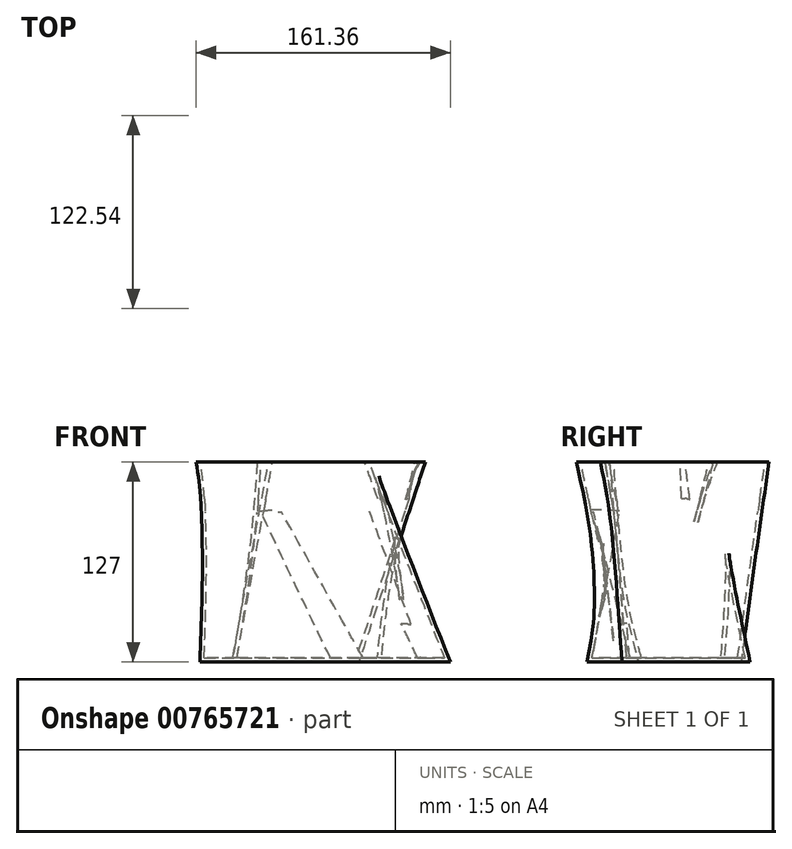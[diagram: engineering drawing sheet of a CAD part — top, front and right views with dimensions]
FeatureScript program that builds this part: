
annotation { "Feature Type Name" : "Feature", "Feature Type Description" : "" }
export const myFeature = defineFeature(function(context is Context, id is Id, definition is map)
    precondition{}
    {
        {
            var Q0;
            Q0=qCreatedBy(makeId("Top.planeOp"),FACE);
            var sketch = newSketch(context, id + "F0", { "sketchPlane" : qUnion([Q0])});
            skFitSpline(sketch, "E0", {"points": [v(0, 44.55) * mm, v(-25.5, 44.55) * mm, v(-44.65, 21.69) * mm, v(-46.6, 0) * mm, v(-53.63, -5.08) * mm, v(-65.55, -33.41) * mm, v(-34.3, -44.16) * mm, v(0, -50.02) * mm, v(31.36, -48.26) * mm, v(33.5, -42) * mm, v(44.84, -19.15) * mm, v(51.1, -18.76) * mm, v(72, -25.8) * mm, v(75.52, -28.33) * mm, v(92.32, -14.85) * mm, v(89.97, -9.18) * mm, v(70.83, 0) * mm, v(67.3, 1.56) * mm, v(34.88, 18.95) * mm, v(47.77, 33.41) * mm, v(37.61, 52.95) * mm, v(14.75, 38.5) * mm, v(12.4, 36.54) * mm, v(0, 44.55) * mm]});
            skSolve(sketch);
        }
        {
            var Q0;
            Q0=qCreatedBy(makeId("Top.planeOp"),FACE);
            cPlane(context, id + "F1", {"entities" : qUnion([Q0]), "cplaneType" : CPlaneType.OFFSET, "offset" : 127 * mm, "width" : 152.4 * mm, "height" : 152.4 * mm});
        }
        {
            var Q0;
            Q0=qCreatedBy(id+"F1.planeOp",FACE);
            var sketch = newSketch(context, id + "F2", { "sketchPlane" : qUnion([Q0])});
            skFitSpline(sketch, "E1", {"points": [v(-29.08, 61.1) * mm, v(-23, 30.98) * mm, v(-59.2, 30.7) * mm, v(-64.17, -7.42) * mm, v(-46.49, -23.17) * mm, v(-36.54, -56.88) * mm, v(12.92, -36.44) * mm, v(42.2, -41.41) * mm, v(50.22, -10.46) * mm, v(77.02, 10.54) * mm, v(34.2, 27.67) * mm, v(20.1, 51.43) * mm, v(-29.08, 61.1) * mm]});
            skSolve(sketch);
        }
        {
            var Q0;
            Q0=makeQuery(id+"F0.imprint","IMPRINT",FACE,{"disambiguationData":[TD([[makeQuery(id+"F0.imprint","IMPRINT",EDGE,{"derivedFrom":sQuery(id+"F0.wireOp",EDGE,"E0")}),1.0]])]});
            var Q1;
            Q1=makeQuery(id+"F2.imprint","IMPRINT",FACE,{"disambiguationData":[TD([[makeQuery(id+"F2.imprint","IMPRINT",EDGE,{"derivedFrom":sQuery(id+"F2.wireOp",EDGE,"E1")}),1.0]])]});
            loft(context, id + "F3", {"sheetProfilesArray" : [{ "sheetProfileEntities" : qUnion([Q0]) }, { "sheetProfileEntities" : qUnion([Q1]) }]});
        }
        {
            var Q0;
            Q0=makeQuery(id+"F3.opLoft","CAP_FACE",FACE,{"disambiguationData":[OSD([makeQuery(id+"F2.imprint","IMPRINT",FACE,{"disambiguationData":[TD([[makeQuery(id+"F2.imprint","IMPRINT",EDGE,{"derivedFrom":sQuery(id+"F2.wireOp",EDGE,"E1")}),1.0]])]})])],"isStart":true});
            shell(context, id + "F4", {"entities" : qUnion([Q0]), "thickness" : 2.54 * mm});
        }
    });
